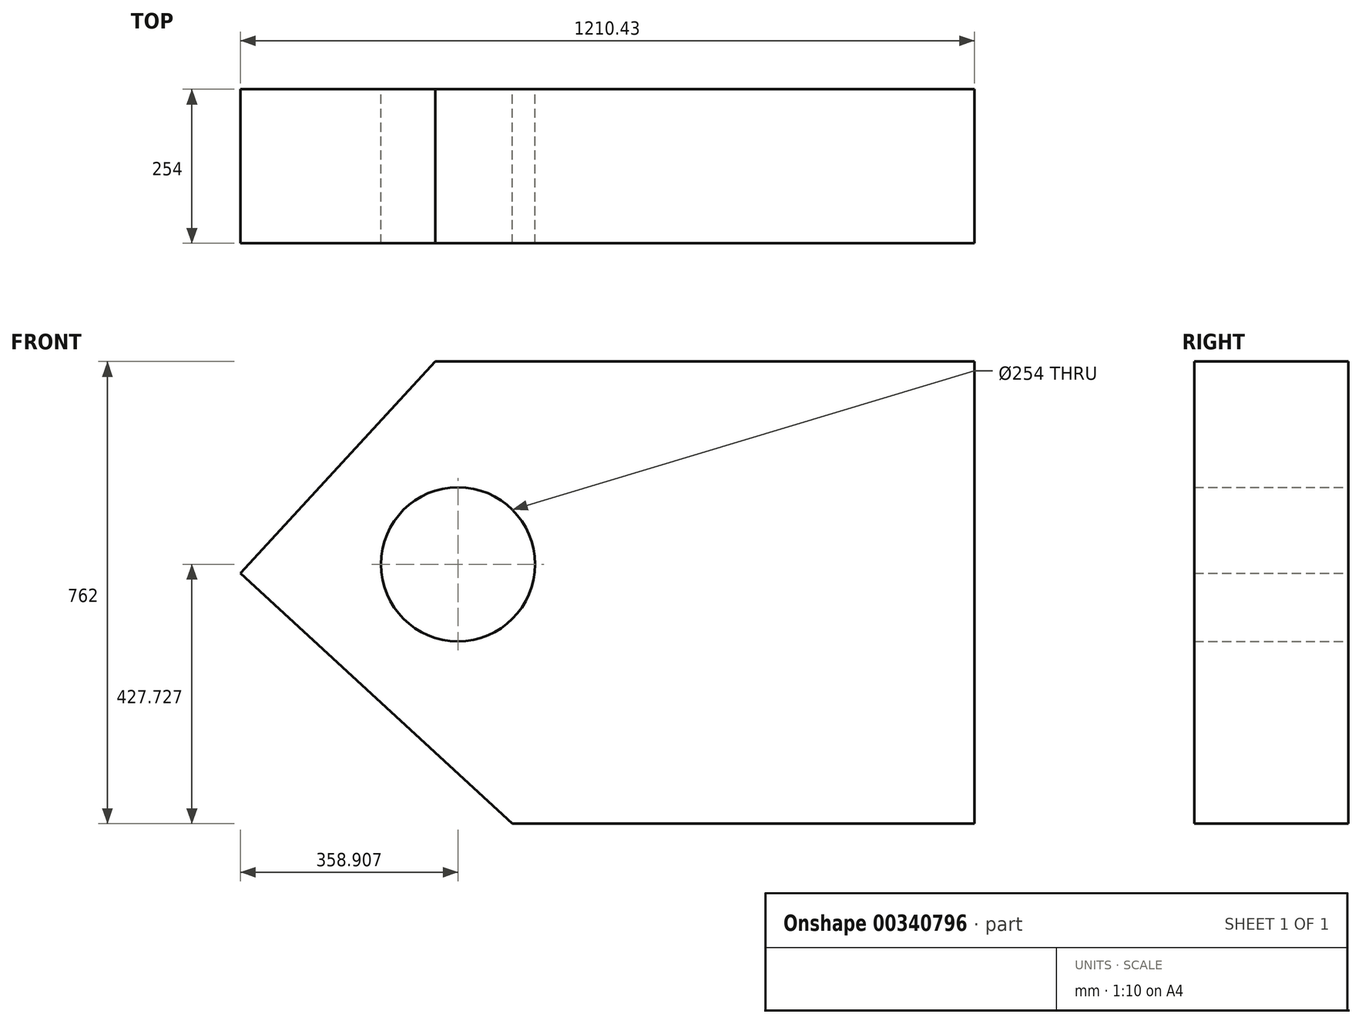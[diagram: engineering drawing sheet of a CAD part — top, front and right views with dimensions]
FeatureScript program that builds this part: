
annotation { "Feature Type Name" : "Feature", "Feature Type Description" : "" }
export const myFeature = defineFeature(function(context is Context, id is Id, definition is map)
    precondition{}
    {
        {
            var Q0;
            Q0=qCreatedBy(makeId("Front.planeOp"),FACE);
            var sketch = newSketch(context, id + "F0", { "sketchPlane" : qUnion([Q0])});
            skLineSegment(sketch, "E0", {"start": v(67.85, -41.81) * mm, "end": v(956.85, -41.81) * mm});
            skLineSegment(sketch, "E1", {"start": v(956.85, -41.81) * mm, "end": v(956.85, -803.81) * mm});
            skLineSegment(sketch, "E2", {"start": v(956.85, -803.81) * mm, "end": v(194.85, -803.81) * mm});
            skLineSegment(sketch, "E3", {"start": v(194.85, -803.81) * mm, "end": v(-253.58, -390.87) * mm});
            skLineSegment(sketch, "E4", {"start": v(-253.58, -390.87) * mm, "end": v(67.85, -41.81) * mm});
            skCircle(sketch, "E5", {"center": v(105.33, -376.08) * mm, "radius": 127 * mm});
            skSolve(sketch);
        }
        {
            var Q0;
            Q0=makeQuery(id+"F0.imprint","IMPRINT",FACE,{"disambiguationData":[TD([[makeQuery(id+"F0.imprint","IMPRINT",EDGE,{"derivedFrom":sQuery(id+"F0.wireOp",EDGE,"E0")}),-1.0]])]});
            extrude(context, id + "F1", {"entities" : qUnion([Q0]), "depth" : 254 * mm});
        }
    });
